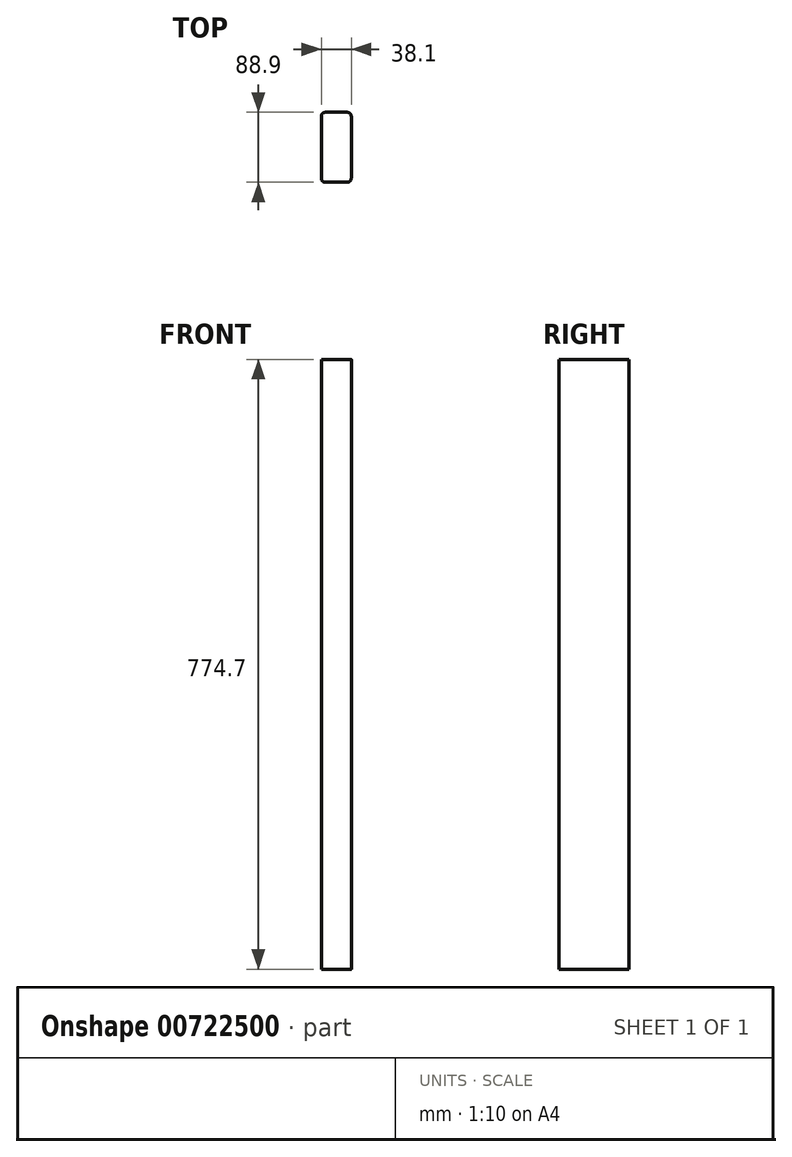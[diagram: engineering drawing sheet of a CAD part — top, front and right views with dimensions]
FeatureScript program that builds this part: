
annotation { "Feature Type Name" : "Feature", "Feature Type Description" : "" }
export const myFeature = defineFeature(function(context is Context, id is Id, definition is map)
    precondition{}
    {
        {
            var Q0;
            Q0=qCreatedBy(makeId("Right.planeOp"),FACE);
            var sketch = newSketch(context, id + "F0", { "sketchPlane" : qUnion([Q0])});
            skLineSegment(sketch, "E0", {"start": v(0, 0) * mm, "end": v(0, -774.7) * mm});
            skLineSegment(sketch, "E1", {"start": v(0, -774.7) * mm, "end": v(88.9, -774.7) * mm});
            skLineSegment(sketch, "E2", {"start": v(88.9, -774.7) * mm, "end": v(88.9, 0) * mm});
            skLineSegment(sketch, "E3", {"start": v(88.9, 0) * mm, "end": v(0, 0) * mm});
            skSolve(sketch);
        }
        {
            var Q0;
            Q0=makeQuery(id+"F0.imprint","IMPRINT",FACE,{"disambiguationData":[TD([[makeQuery(id+"F0.imprint","IMPRINT",EDGE,{"derivedFrom":sQuery(id+"F0.wireOp",EDGE,"E0")}),1.0]])]});
            extrude(context, id + "F1", {"entities" : qUnion([Q0]), "depth" : 38.1 * mm, "offsetDistance" : 25.4 * mm});
        }
        {
            var Q0;
            Q0=makeQuery(id+"F1.opExtrude","CAP_EDGE",EDGE,{"disambiguationData":[OSD([sQuery(id+"F0.wireOp",EDGE,"E0")])],"isStart":false});
            var Q1;
            Q1=makeQuery(id+"F1.opExtrude","CAP_EDGE",EDGE,{"disambiguationData":[OSD([sQuery(id+"F0.wireOp",EDGE,"E0")])],"isStart":true});
            var Q2;
            Q2=makeQuery(id+"F1.opExtrude","CAP_EDGE",EDGE,{"disambiguationData":[OSD([sQuery(id+"F0.wireOp",EDGE,"E2")])],"isStart":false});
            var Q3;
            Q3=makeQuery(id+"F1.opExtrude","CAP_EDGE",EDGE,{"disambiguationData":[OSD([sQuery(id+"F0.wireOp",EDGE,"E2")])],"isStart":true});
            fillet(context, id + "F2", {"entities" : qUnion([Q0, Q1, Q2, Q3]), "radius" : 5.08 * mm, "tangentPropagation" : true, "allowEdgeOverflow" : false});
        }
    });
